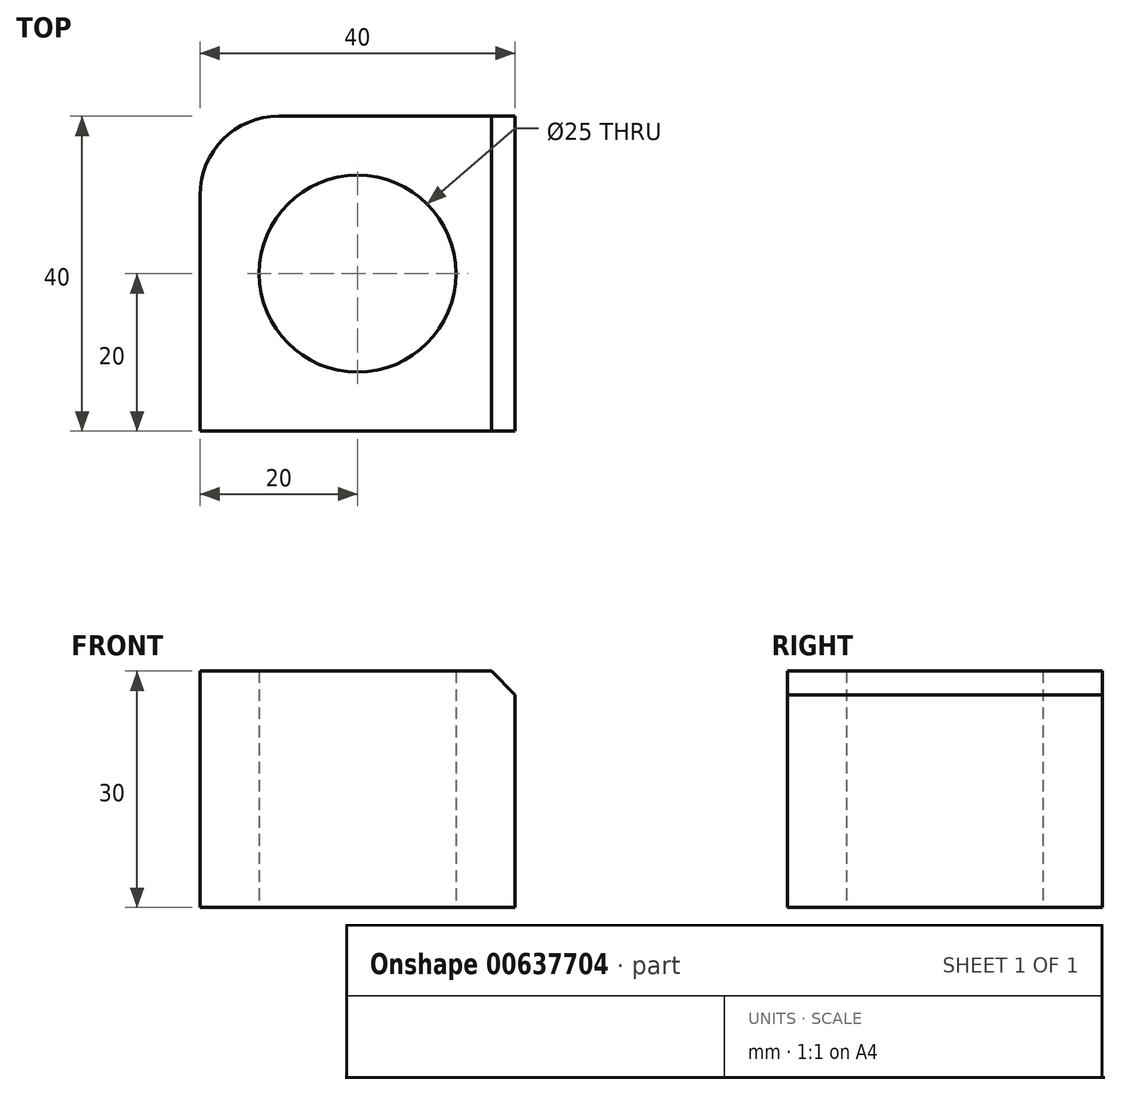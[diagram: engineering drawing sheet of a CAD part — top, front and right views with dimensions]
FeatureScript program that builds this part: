
annotation { "Feature Type Name" : "Feature", "Feature Type Description" : "" }
export const myFeature = defineFeature(function(context is Context, id is Id, definition is map)
    precondition{}
    {
        {
            var Q0;
            Q0=qCreatedBy(makeId("Top.planeOp"),FACE);
            var sketch = newSketch(context, id + "F0", { "sketchPlane" : qUnion([Q0])});
            skLineSegment(sketch, "E0", {"start": v(0, 0) * mm, "end": v(0, 10) * mm});
            skLineSegment(sketch, "E1", {"start": v(10, 20) * mm, "end": v(40, 20) * mm});
            skLineSegment(sketch, "E2", {"start": v(40, 20) * mm, "end": v(40, 0) * mm});
            skLineSegment(sketch, "E3", {"start": v(0, 0) * mm, "end": v(40, 0) * mm, "construction": true});
            skLineSegment(sketch, "E4.MirrorCS", {"start": v(40, -20) * mm, "end": v(40, 0) * mm});
            skLineSegment(sketch, "E5.MirrorCS", {"start": v(0, -20) * mm, "end": v(40, -20) * mm});
            skLineSegment(sketch, "E6.MirrorCS", {"start": v(0, 0) * mm, "end": v(0, -20) * mm});
            skCircle(sketch, "E7", {"center": v(20, 0) * mm, "radius": 12.5 * mm});
            skPoint(sketch, "E8.visualSharp", {"position": v(0, 20) * mm});
            skArc(sketch, "E8.filletArc", {"start": v(10, 20) * mm, "mid": v(2.93, 17.07) * mm, "end": v(0, 10) * mm});
            skSolve(sketch);
        }
        {
            var Q0;
            Q0=makeQuery(id+"F0.imprint","IMPRINT",FACE,{"disambiguationData":[TD([[makeQuery(id+"F0.imprint","IMPRINT",EDGE,{"derivedFrom":sQuery(id+"F0.wireOp",EDGE,"E0")}),-1.0]])]});
            extrude(context, id + "F1", {"entities" : qUnion([Q0]), "depth" : 30 * mm, "offsetDistance" : 25 * mm});
        }
        {
            var Q0;
            Q0=makeQuery(id+"F1.opExtrude","CAP_EDGE",EDGE,{"disambiguationData":[OSD([sQuery(id+"F0.wireOp",EDGE,"E2"),sQuery(id+"F0.wireOp",EDGE,"E4.MirrorCS")])],"isStart":false});
            chamfer(context, id + "F2", {"entities" : qUnion([Q0]), "width" : 3 * mm, "tangentPropagation" : true});
        }
    });
